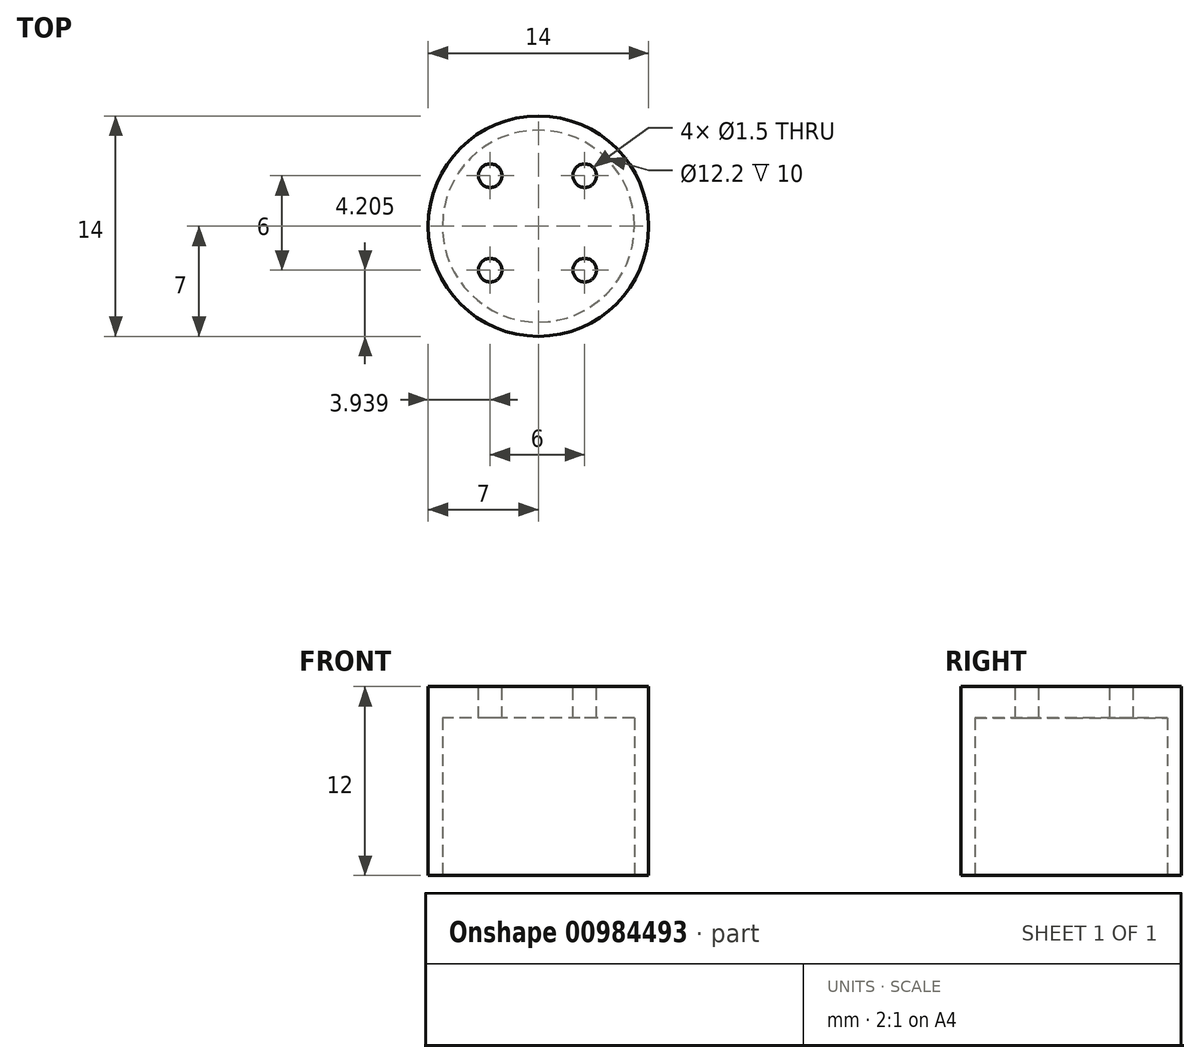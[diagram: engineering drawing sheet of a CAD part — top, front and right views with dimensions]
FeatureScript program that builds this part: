
annotation { "Feature Type Name" : "Feature", "Feature Type Description" : "" }
export const myFeature = defineFeature(function(context is Context, id is Id, definition is map)
    precondition{}
    {
        {
            var Q0;
            Q0=qCreatedBy(makeId("Top.planeOp"),FACE);
            var sketch = newSketch(context, id + "F0", { "sketchPlane" : qUnion([Q0])});
            skCircle(sketch, "E0", {"center": v(0, 0) * mm, "radius": 6.1 * mm});
            skCircle(sketch, "E1", {"center": v(0, 0) * mm, "radius": 7 * mm});
            skSolve(sketch);
        }
        {
            var Q0;
            Q0 = qSketchRegion(id + "F0", true);
            extrude(context, id + "F1", {"entities" : qUnion([Q0]), "depth" : 10 * mm, "offsetDistance" : 25 * mm});
        }
        {
            var Q0;
            Q0=makeQuery(id+"F1.opExtrude","CAP_FACE",FACE,{"disambiguationData":[OSD([sQuery(id+"F0.wireOp",EDGE,"E0"),sQuery(id+"F0.wireOp",EDGE,"E1")])],"isStart":false});
            var sketch = newSketch(context, id + "F2", { "sketchPlane" : qUnion([Q0])});
            skCircle(sketch, "E2", {"center": v(0, 0) * mm, "radius": 7 * mm});
            skSolve(sketch);
        }
        {
            var Q0;
            Q0 = qSketchRegion(id + "F2", true);
            extrude(context, id + "F3", {"entities" : qUnion([Q0]), "operationType" : NewBodyOperationType.ADD, "depth" : 2 * mm, "offsetDistance" : 25 * mm});
        }
        {
            var Q0;
            Q0=makeQuery(id+"F3.opExtrude","CAP_FACE",FACE,{"disambiguationData":[OSD([sQuery(id+"F2.wireOp",EDGE,"E2")])],"isStart":false});
            var sketch = newSketch(context, id + "F4", { "sketchPlane" : qUnion([Q0])});
            skCircle(sketch, "E3", {"center": v(2.94, -2.8) * mm, "radius": 0.75 * mm});
            skCircle(sketch, "E4.0.1.0", {"center": v(2.94, 3.2) * mm, "radius": 0.75 * mm});
            skCircle(sketch, "E4.1.0.0", {"center": v(-3.06, -2.8) * mm, "radius": 0.75 * mm});
            skCircle(sketch, "E4.1.1.0", {"center": v(-3.06, 3.2) * mm, "radius": 0.75 * mm});
            skLineSegment(sketch, "E4.direction1", {"start": v(2.94, -2.8) * mm, "end": v(-3.06, -2.8) * mm, "construction": true});
            skLineSegment(sketch, "E4.direction2", {"start": v(2.94, -2.8) * mm, "end": v(2.94, 3.2) * mm, "construction": true});
            skSolve(sketch);
        }
        {
            var Q0;
            Q0 = qSketchRegion(id + "F4", true);
            var Q1;
            Q1=makeQuery(id+"F3.opExtrude","CAP_FACE",FACE,{"disambiguationData":[OSD([sQuery(id+"F2.wireOp",EDGE,"E2")])],"isStart":true});
            extrude(context, id + "F5", {"entities" : qUnion([Q0]), "operationType" : NewBodyOperationType.REMOVE, "endBound" : BoundingType.UP_TO_SURFACE, "oppositeDirection" : true, "depth" : 25 * mm, "endBoundEntityFace" : qUnion([Q1]), "offsetDistance" : 25 * mm});
        }
    });
